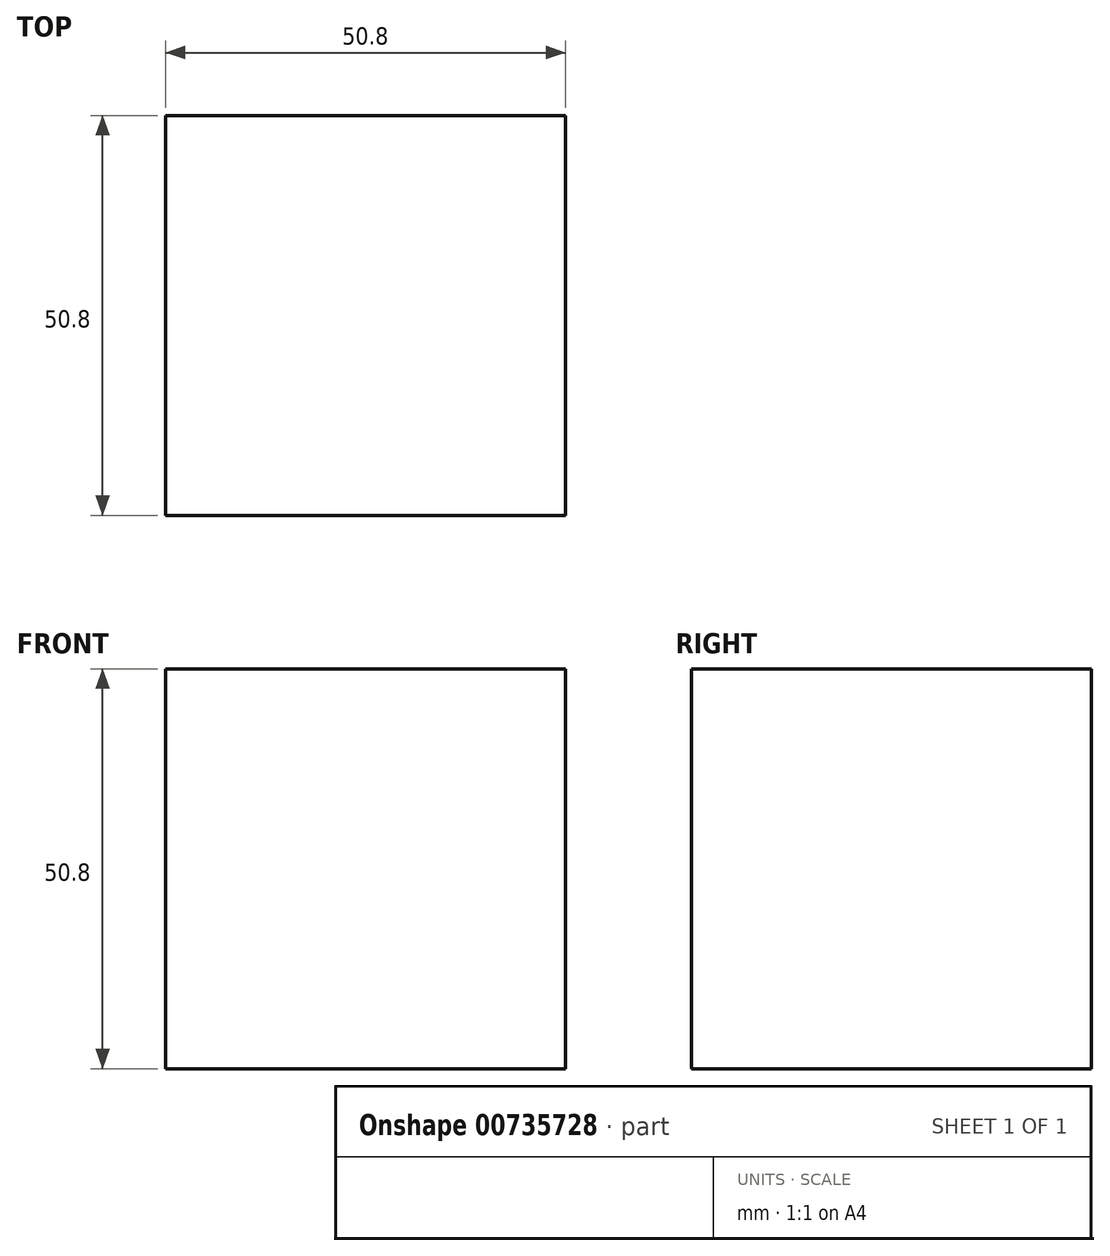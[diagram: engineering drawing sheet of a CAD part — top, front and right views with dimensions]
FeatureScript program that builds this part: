
annotation { "Feature Type Name" : "Feature", "Feature Type Description" : "" }
export const myFeature = defineFeature(function(context is Context, id is Id, definition is map)
    precondition{}
    {
        {
            var Q0;
            Q0=qCreatedBy(makeId("Front.planeOp"),FACE);
            var sketch = newSketch(context, id + "F0", { "sketchPlane" : qUnion([Q0])});
            skLineSegment(sketch, "E0", {"start": v(0, 0) * mm, "end": v(0, 50.8) * mm});
            skLineSegment(sketch, "E1", {"start": v(0, 50.8) * mm, "end": v(50.8, 50.8) * mm});
            skLineSegment(sketch, "E2", {"start": v(50.8, 50.8) * mm, "end": v(50.8, 0) * mm});
            skLineSegment(sketch, "E3", {"start": v(50.8, 0) * mm, "end": v(0, 0) * mm});
            skSolve(sketch);
        }
        {
            var Q0;
            Q0=makeQuery(id+"F0.imprint","IMPRINT",FACE,{"disambiguationData":[TD([[makeQuery(id+"F0.imprint","IMPRINT",EDGE,{"derivedFrom":sQuery(id+"F0.wireOp",EDGE,"E0")}),-1.0]])]});
            extrude(context, id + "F1", {"entities" : qUnion([Q0]), "depth" : 50.8 * mm, "offsetDistance" : 25.4 * mm});
        }
    });
